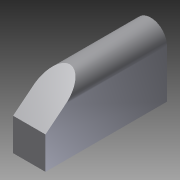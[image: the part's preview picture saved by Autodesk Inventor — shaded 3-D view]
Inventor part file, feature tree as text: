
AUTODESK INVENTOR PART (.ipt)
format: ipt  version: 2012 (Build 160160000, 160)  size: 88,064 bytes
history: native  units: in
note: dims shown in document units (in); Inventor stores cm internally (conversion verified against a paired STEP export)
features: extrude x2, sketch x2
ambient origin geometry x8: Origin, YZ Plane, XZ Plane, XY Plane, X Axis, Y Axis, Z Axis, Center Point
bodies: Solid1 (feature_tree)
feature tree (4):
  extrude  "Extrusion1"  Depth=0.3in
  extrude  "Extrusion2"  Depth=0.5in
  sketch  "Sketch1"  dims[d0=0.2in d1=0.3in]
  sketch  "Sketch2"  dims[d2=0.75in d3=0.0in d4=0.5in d5=0.2in d6=0.1in d7=0.75in d8=0.0in]
